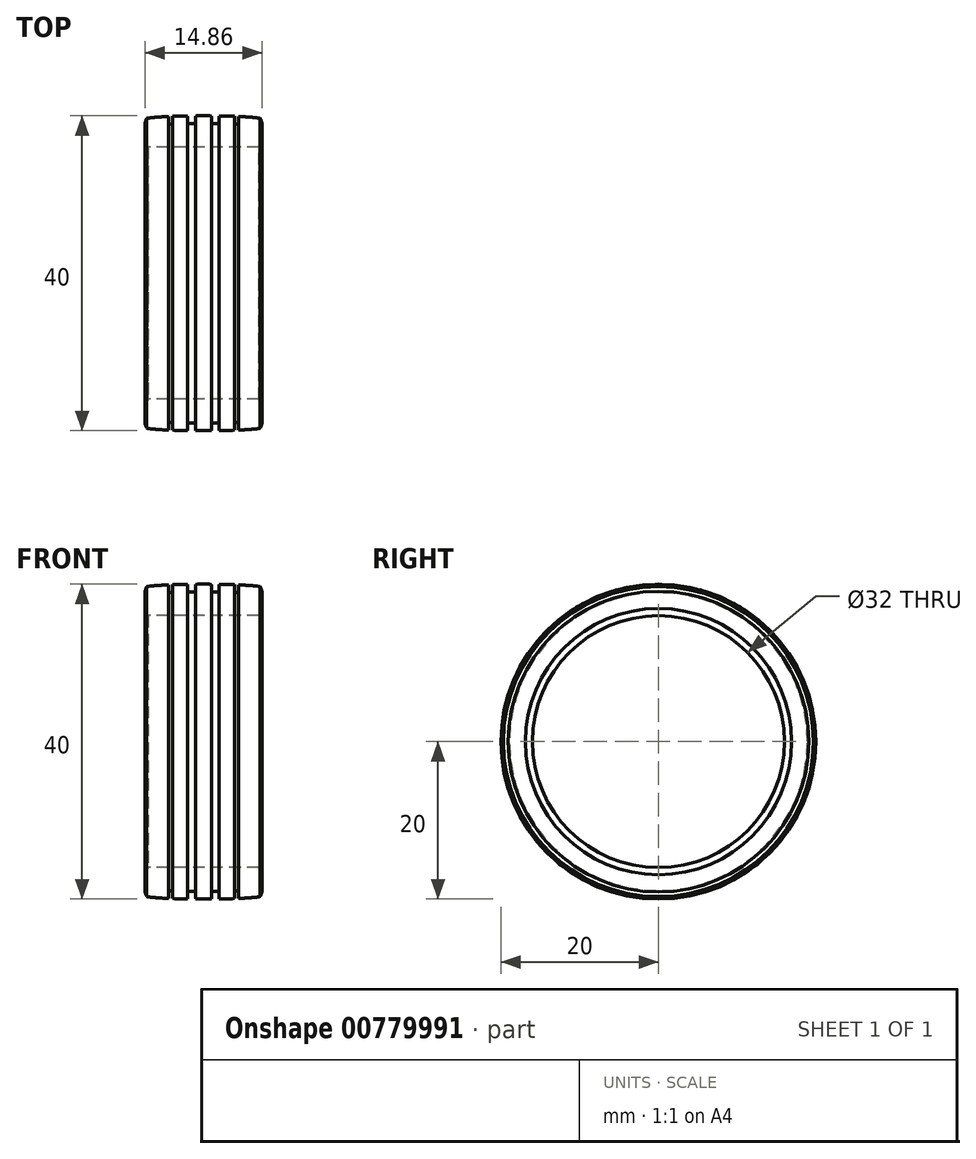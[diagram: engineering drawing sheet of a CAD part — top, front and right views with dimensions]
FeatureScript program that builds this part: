
annotation { "Feature Type Name" : "Feature", "Feature Type Description" : "" }
export const myFeature = defineFeature(function(context is Context, id is Id, definition is map)
    precondition{}
    {
        {
            var Q0;
            Q0=qCreatedBy(makeId("Front.planeOp"),FACE);
            var sketch = newSketch(context, id + "F0", { "sketchPlane" : qUnion([Q0])});
            skLineSegment(sketch, "E0", {"start": v(0, 0) * mm, "end": v(7.05, 0) * mm});
            skLineSegment(sketch, "E1", {"start": v(0, 3.57) * mm, "end": v(0, 4) * mm});
            skArc(sketch, "E2", {"start": v(7.43, 3.1) * mm, "mid": v(7.33, 3.4) * mm, "end": v(7.21, 3.69) * mm});
            skPoint(sketch, "E3", {"position": v(7.43, 2) * mm});
            skLineSegment(sketch, "E4", {"start": v(7.43, 2) * mm, "end": v(7.43, 0.9) * mm});
            skLineSegment(sketch, "E5.MirrorCS", {"start": v(7.43, 2) * mm, "end": v(7.43, 3.1) * mm});
            skArc(sketch, "E6.trimOffspring", {"start": v(7.05, 0) * mm, "mid": v(7.27, 0.44) * mm, "end": v(7.43, 0.9) * mm});
            skEllipticalArc(sketch, "E7.trimOffspring", {});
            skLineSegment(sketch, "E8", {"start": v(1, 4) * mm, "end": v(1, 3) * mm});
            skLineSegment(sketch, "E9", {"start": v(1, 3) * mm, "end": v(2, 3) * mm});
            skLineSegment(sketch, "E10", {"start": v(2, 3) * mm, "end": v(2, 3.98) * mm});
            skEllipticalArc(sketch, "E11.trimOffspring", {});
            skLineSegment(sketch, "E12", {"start": v(3.93, 3.94) * mm, "end": v(3.93, 2.94) * mm});
            skLineSegment(sketch, "E13", {"start": v(3.93, 2.94) * mm, "end": v(4.43, 2.94) * mm});
            skLineSegment(sketch, "E14", {"start": v(4.43, 2.94) * mm, "end": v(4.43, 3.92) * mm});
            skEllipticalArc(sketch, "E15.trimOffspring", {});
            skLineSegment(sketch, "E16.MirrorCS", {"start": v(0, 0) * mm, "end": v(-7.05, 0) * mm});
            skEllipticalArc(sketch, "E17.MirrorCS", {});
            skLineSegment(sketch, "E18.MirrorCS", {"start": v(-1, 4) * mm, "end": v(-1, 3) * mm});
            skLineSegment(sketch, "E19.MirrorCS", {"start": v(-1, 3) * mm, "end": v(-2, 3) * mm});
            skLineSegment(sketch, "E20.MirrorCS", {"start": v(-2, 3) * mm, "end": v(-2, 3.98) * mm});
            skEllipticalArc(sketch, "E21.MirrorCS", {});
            skLineSegment(sketch, "E22.MirrorCS", {"start": v(-3.93, 3.94) * mm, "end": v(-3.93, 2.94) * mm});
            skLineSegment(sketch, "E23.MirrorCS", {"start": v(-3.93, 2.94) * mm, "end": v(-4.43, 2.94) * mm});
            skLineSegment(sketch, "E24.MirrorCS", {"start": v(-4.43, 2.94) * mm, "end": v(-4.43, 3.92) * mm});
            skEllipticalArc(sketch, "E25.MirrorCS", {});
            skArc(sketch, "E26.MirrorCS", {"start": v(-7.43, 3.1) * mm, "mid": v(-7.33, 3.4) * mm, "end": v(-7.21, 3.69) * mm});
            skLineSegment(sketch, "E27.MirrorCS", {"start": v(-7.43, 2) * mm, "end": v(-7.43, 3.1) * mm});
            skLineSegment(sketch, "E28.MirrorCS", {"start": v(-7.43, 2) * mm, "end": v(-7.43, 0.9) * mm});
            skArc(sketch, "E29.MirrorCS", {"start": v(-7.05, 0) * mm, "mid": v(-7.27, 0.44) * mm, "end": v(-7.43, 0.9) * mm});
            skLineSegment(sketch, "E30", {"start": v(-13.74, -16) * mm, "end": v(18.33, -16) * mm});
            const initialGuessF0  = {"E7.trimOffspring": [0, 0.003568643471226096, 1, 0, 0.007492060773074626, 0.00043135652877390393, 0.27496202603151304, 0.9384907722704857], "E11.trimOffspring": [0, 0.003568643471226096, 1, 0, 0.007492060773074626, 0.00043135652877390393, 1.4369221717183425, 1.5707963267948966], "E15.trimOffspring": [0, 0.003568643471226096, 1, 0, 0.007492060773074626, 0.00043135652877390393, 1.0189400727703717, 1.3005703191943803], "E17.MirrorCS": [0, 0.003568643471226096, -1, 0, 0.007492060773074626, 0.00043135652877390393, 4.71238898038469, 4.8462631354612435], "E21.MirrorCS": [0, 0.003568643471226096, -1, 0, 0.007492060773074626, 0.00043135652877390393, 4.982614987985206, 5.2642452344092145], "E25.MirrorCS": [0, 0.003568643471226096, -1, 0, 0.007492060773074626, 0.00043135652877390393, 5.344694534909101, 6.008223281148073]};
            skSetInitialGuess(sketch, initialGuessF0);
            skSolve(sketch);
        }
        {
            var Q0;
            Q0=makeQuery(id+"F0.imprint","IMPRINT",FACE,{"disambiguationData":[TD([[makeQuery(id+"F0.imprint","IMPRINT",EDGE,{"derivedFrom":sQuery(id+"F0.wireOp",EDGE,"E0")}),1.0]])]});
            var Q1;
            Q1=sQuery(id+"F0.wireOp",EDGE,"E30");
            revolve(context, id + "F1", {"surfaceOperationType" : NewSurfaceOperationType.NEW, "entities" : qUnion([Q0]), "axis" : qUnion([Q1]), "revolveType" : RevolveType.FULL});
        }
    });
